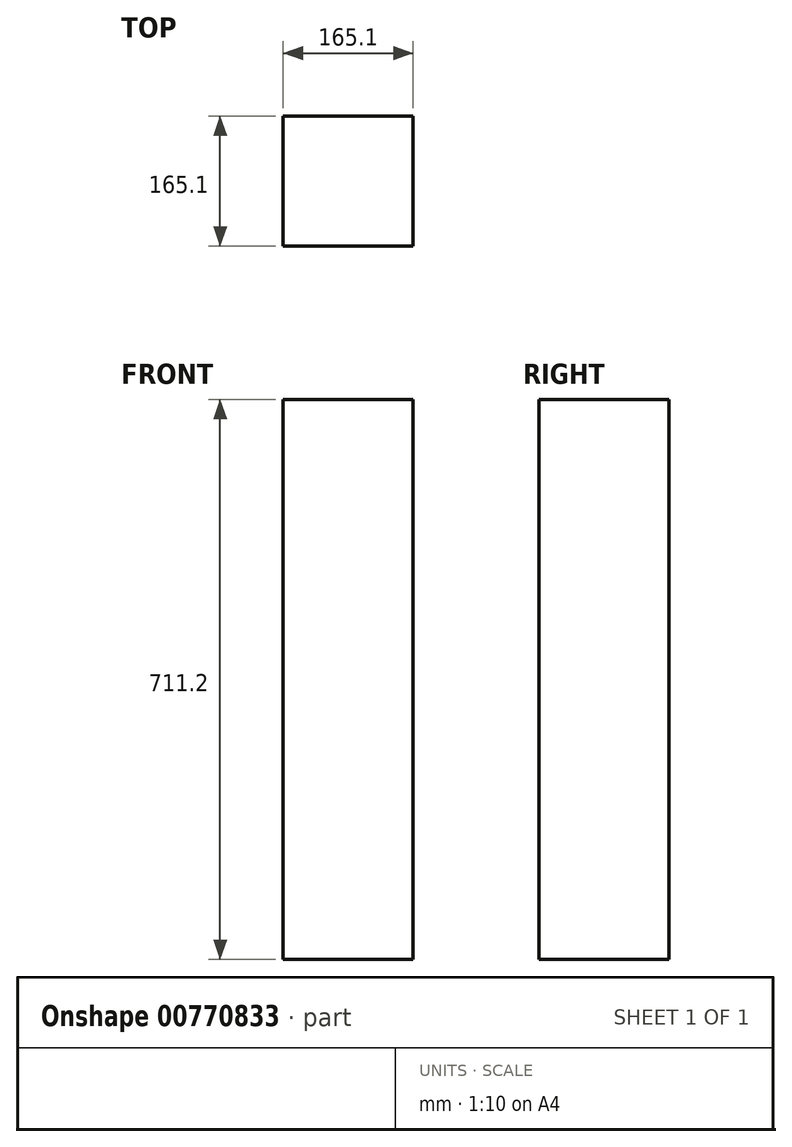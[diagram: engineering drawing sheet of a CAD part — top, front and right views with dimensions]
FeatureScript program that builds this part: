
annotation { "Feature Type Name" : "Feature", "Feature Type Description" : "" }
export const myFeature = defineFeature(function(context is Context, id is Id, definition is map)
    precondition{}
    {
        {
            var Q0;
            Q0=qCreatedBy(makeId("Top.planeOp"),FACE);
            var sketch = newSketch(context, id + "F0", { "sketchPlane" : qUnion([Q0])});
            skLineSegment(sketch, "E0.bottom", {"start": v(-82.55, -82.55) * mm, "end": v(82.55, -82.55) * mm});
            skLineSegment(sketch, "E0.top", {"start": v(-82.55, 82.55) * mm, "end": v(82.55, 82.55) * mm});
            skLineSegment(sketch, "E0.left", {"start": v(-82.55, -82.55) * mm, "end": v(-82.55, 82.55) * mm});
            skLineSegment(sketch, "E0.right", {"start": v(82.55, -82.55) * mm, "end": v(82.55, 82.55) * mm});
            skPoint(sketch, "E0.middle", {"position": v(0, 0) * mm});
            skSolve(sketch);
        }
        {
            var Q0;
            Q0 = qSketchRegion(id + "F0", true);
            extrude(context, id + "F1", {"entities" : qUnion([Q0]), "depth" : 711.2 * mm, "offsetDistance" : 25.4 * mm});
        }
    });
